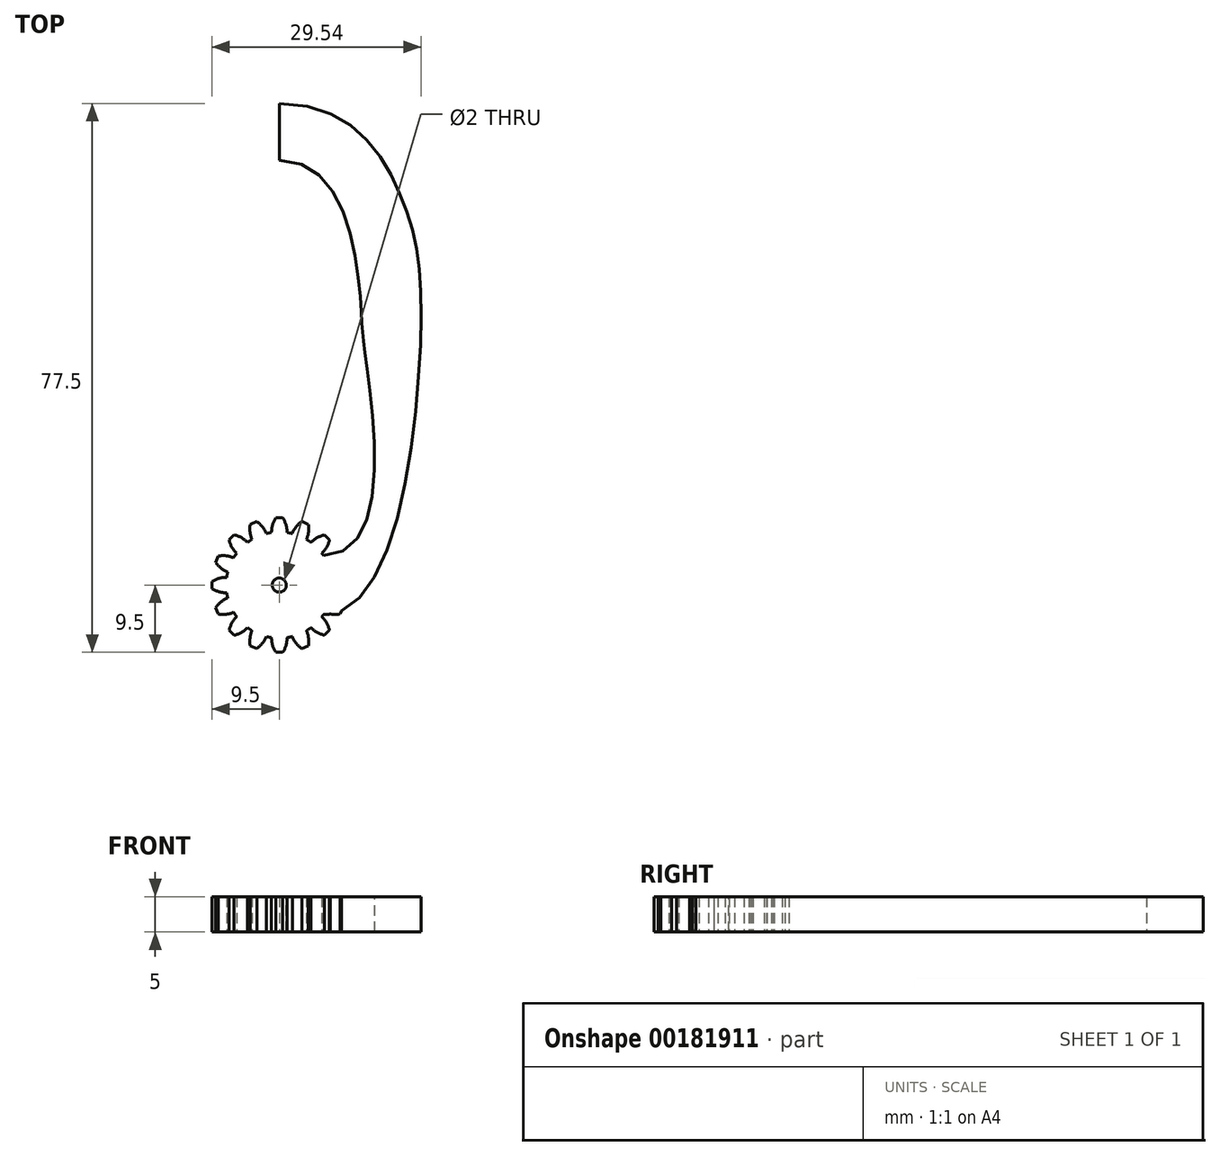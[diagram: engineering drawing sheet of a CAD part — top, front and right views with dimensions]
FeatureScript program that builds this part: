
annotation { "Feature Type Name" : "Feature", "Feature Type Description" : "" }
export const myFeature = defineFeature(function(context is Context, id is Id, definition is map)
    precondition{}
    {
        {
            var Q0;
            Q0=qCreatedBy(makeId("Top.planeOp"),FACE);
            var sketch = newSketch(context, id + "F0", { "sketchPlane" : qUnion([Q0])});
            skCircle(sketch, "E0", {"center": v(0, 0) * mm, "radius": 7.5 * mm});
            skLineSegment(sketch, "E1", {"start": v(0, 0) * mm, "end": v(0, 7.5) * mm, "construction": true});
            skLineSegment(sketch, "E2", {"start": v(0, 9.5) * mm, "end": v(-0.5, 9.5) * mm});
            skArc(sketch, "E3", {"start": v(-0.5, 9.5) * mm, "mid": v(-0.95, 8.5) * mm, "end": v(-1.09, 7.42) * mm});
            skLineSegment(sketch, "E4.MirrorCS", {"start": v(0, 9.5) * mm, "end": v(0.5, 9.5) * mm});
            skArc(sketch, "E5.MirrorCS", {"start": v(0.5, 9.5) * mm, "mid": v(0.95, 8.5) * mm, "end": v(1.09, 7.42) * mm});
            skArc(sketch, "E6.1.0", {"start": v(-4.1, 8.59) * mm, "mid": v(-4.13, 7.5) * mm, "end": v(-3.85, 6.44) * mm});
            skLineSegment(sketch, "E6.1.1", {"start": v(-3.64, 8.78) * mm, "end": v(-4.1, 8.59) * mm});
            skLineSegment(sketch, "E6.1.2", {"start": v(-3.64, 8.78) * mm, "end": v(-3.17, 8.97) * mm});
            skArc(sketch, "E6.1.3", {"start": v(-3.17, 8.97) * mm, "mid": v(-2.38, 8.22) * mm, "end": v(-1.83, 7.27) * mm});
            skArc(sketch, "E6.2.0", {"start": v(-7.07, 6.36) * mm, "mid": v(-6.69, 5.34) * mm, "end": v(-6.02, 4.48) * mm});
            skLineSegment(sketch, "E6.2.1", {"start": v(-6.72, 6.72) * mm, "end": v(-7.07, 6.36) * mm});
            skLineSegment(sketch, "E6.2.2", {"start": v(-6.72, 6.72) * mm, "end": v(-6.36, 7.07) * mm});
            skArc(sketch, "E6.2.3", {"start": v(-6.36, 7.07) * mm, "mid": v(-5.34, 6.69) * mm, "end": v(-4.48, 6.02) * mm});
            skArc(sketch, "E6.3.0", {"start": v(-8.97, 3.17) * mm, "mid": v(-8.22, 2.38) * mm, "end": v(-7.27, 1.83) * mm});
            skLineSegment(sketch, "E6.3.1", {"start": v(-8.78, 3.64) * mm, "end": v(-8.97, 3.17) * mm});
            skLineSegment(sketch, "E6.3.2", {"start": v(-8.78, 3.64) * mm, "end": v(-8.59, 4.1) * mm});
            skArc(sketch, "E6.3.3", {"start": v(-8.59, 4.1) * mm, "mid": v(-7.5, 4.13) * mm, "end": v(-6.44, 3.85) * mm});
            skArc(sketch, "E6.4.0", {"start": v(-9.5, -0.5) * mm, "mid": v(-8.5, -0.95) * mm, "end": v(-7.42, -1.09) * mm});
            skLineSegment(sketch, "E6.4.1", {"start": v(-9.5, 0) * mm, "end": v(-9.5, -0.5) * mm});
            skLineSegment(sketch, "E6.4.2", {"start": v(-9.5, 0) * mm, "end": v(-9.5, 0.5) * mm});
            skArc(sketch, "E6.4.3", {"start": v(-9.5, 0.5) * mm, "mid": v(-8.5, 0.95) * mm, "end": v(-7.42, 1.09) * mm});
            skArc(sketch, "E6.5.0", {"start": v(-8.59, -4.1) * mm, "mid": v(-7.5, -4.13) * mm, "end": v(-6.44, -3.85) * mm});
            skLineSegment(sketch, "E6.5.1", {"start": v(-8.78, -3.64) * mm, "end": v(-8.59, -4.1) * mm});
            skLineSegment(sketch, "E6.5.2", {"start": v(-8.78, -3.64) * mm, "end": v(-8.97, -3.17) * mm});
            skArc(sketch, "E6.5.3", {"start": v(-8.97, -3.17) * mm, "mid": v(-8.22, -2.38) * mm, "end": v(-7.27, -1.83) * mm});
            skArc(sketch, "E6.6.0", {"start": v(-6.36, -7.07) * mm, "mid": v(-5.34, -6.69) * mm, "end": v(-4.48, -6.02) * mm});
            skLineSegment(sketch, "E6.6.1", {"start": v(-6.72, -6.72) * mm, "end": v(-6.36, -7.07) * mm});
            skLineSegment(sketch, "E6.6.2", {"start": v(-6.72, -6.72) * mm, "end": v(-7.07, -6.36) * mm});
            skArc(sketch, "E6.6.3", {"start": v(-7.07, -6.36) * mm, "mid": v(-6.69, -5.34) * mm, "end": v(-6.02, -4.48) * mm});
            skArc(sketch, "E6.7.0", {"start": v(-3.17, -8.97) * mm, "mid": v(-2.38, -8.22) * mm, "end": v(-1.83, -7.27) * mm});
            skLineSegment(sketch, "E6.7.1", {"start": v(-3.64, -8.78) * mm, "end": v(-3.17, -8.97) * mm});
            skLineSegment(sketch, "E6.7.2", {"start": v(-3.64, -8.78) * mm, "end": v(-4.1, -8.59) * mm});
            skArc(sketch, "E6.7.3", {"start": v(-4.1, -8.59) * mm, "mid": v(-4.13, -7.5) * mm, "end": v(-3.85, -6.44) * mm});
            skArc(sketch, "E6.8.0", {"start": v(0.5, -9.5) * mm, "mid": v(0.95, -8.5) * mm, "end": v(1.09, -7.42) * mm});
            skLineSegment(sketch, "E6.8.1", {"start": v(0, -9.5) * mm, "end": v(0.5, -9.5) * mm});
            skLineSegment(sketch, "E6.8.2", {"start": v(0, -9.5) * mm, "end": v(-0.5, -9.5) * mm});
            skArc(sketch, "E6.8.3", {"start": v(-0.5, -9.5) * mm, "mid": v(-0.95, -8.5) * mm, "end": v(-1.09, -7.42) * mm});
            skArc(sketch, "E6.9.0", {"start": v(4.1, -8.59) * mm, "mid": v(4.13, -7.5) * mm, "end": v(3.85, -6.44) * mm});
            skLineSegment(sketch, "E6.9.1", {"start": v(3.64, -8.78) * mm, "end": v(4.1, -8.59) * mm});
            skLineSegment(sketch, "E6.9.2", {"start": v(3.64, -8.78) * mm, "end": v(3.17, -8.97) * mm});
            skArc(sketch, "E6.9.3", {"start": v(3.17, -8.97) * mm, "mid": v(2.38, -8.22) * mm, "end": v(1.83, -7.27) * mm});
            skArc(sketch, "E6.10.0", {"start": v(7.07, -6.36) * mm, "mid": v(6.69, -5.34) * mm, "end": v(6.02, -4.48) * mm});
            skLineSegment(sketch, "E6.10.1", {"start": v(6.72, -6.72) * mm, "end": v(7.07, -6.36) * mm});
            skLineSegment(sketch, "E6.10.2", {"start": v(6.72, -6.72) * mm, "end": v(6.36, -7.07) * mm});
            skArc(sketch, "E6.10.3", {"start": v(6.36, -7.07) * mm, "mid": v(5.34, -6.69) * mm, "end": v(4.48, -6.02) * mm});
            skArc(sketch, "E6.11.0", {"start": v(8.97, -3.17) * mm, "mid": v(8.22, -2.38) * mm, "end": v(7.27, -1.83) * mm});
            skLineSegment(sketch, "E6.11.1", {"start": v(8.78, -3.64) * mm, "end": v(8.97, -3.17) * mm});
            skLineSegment(sketch, "E6.11.2", {"start": v(8.78, -3.64) * mm, "end": v(8.59, -4.1) * mm});
            skArc(sketch, "E6.11.3", {"start": v(8.59, -4.1) * mm, "mid": v(7.5, -4.13) * mm, "end": v(6.44, -3.85) * mm});
            skArc(sketch, "E6.12.0", {"start": v(9.5, 0.5) * mm, "mid": v(8.5, 0.95) * mm, "end": v(7.42, 1.09) * mm});
            skLineSegment(sketch, "E6.12.1", {"start": v(9.5, 0) * mm, "end": v(9.5, 0.5) * mm});
            skLineSegment(sketch, "E6.12.2", {"start": v(9.5, 0) * mm, "end": v(9.5, -0.5) * mm});
            skArc(sketch, "E6.12.3", {"start": v(9.5, -0.5) * mm, "mid": v(8.5, -0.95) * mm, "end": v(7.42, -1.09) * mm});
            skArc(sketch, "E6.13.0", {"start": v(8.59, 4.1) * mm, "mid": v(7.5, 4.13) * mm, "end": v(6.44, 3.85) * mm});
            skLineSegment(sketch, "E6.13.1", {"start": v(8.78, 3.64) * mm, "end": v(8.59, 4.1) * mm});
            skLineSegment(sketch, "E6.13.2", {"start": v(8.78, 3.64) * mm, "end": v(8.97, 3.17) * mm});
            skArc(sketch, "E6.13.3", {"start": v(8.97, 3.17) * mm, "mid": v(8.22, 2.38) * mm, "end": v(7.27, 1.83) * mm});
            skArc(sketch, "E6.14.0", {"start": v(6.36, 7.07) * mm, "mid": v(5.34, 6.69) * mm, "end": v(4.48, 6.02) * mm});
            skLineSegment(sketch, "E6.14.1", {"start": v(6.72, 6.72) * mm, "end": v(6.36, 7.07) * mm});
            skLineSegment(sketch, "E6.14.2", {"start": v(6.72, 6.72) * mm, "end": v(7.07, 6.36) * mm});
            skArc(sketch, "E6.14.3", {"start": v(7.07, 6.36) * mm, "mid": v(6.69, 5.34) * mm, "end": v(6.02, 4.48) * mm});
            skArc(sketch, "E6.15.0", {"start": v(3.17, 8.97) * mm, "mid": v(2.38, 8.22) * mm, "end": v(1.83, 7.27) * mm});
            skLineSegment(sketch, "E6.15.1", {"start": v(3.64, 8.78) * mm, "end": v(3.17, 8.97) * mm});
            skLineSegment(sketch, "E6.15.2", {"start": v(3.64, 8.78) * mm, "end": v(4.1, 8.59) * mm});
            skArc(sketch, "E6.15.3", {"start": v(4.1, 8.59) * mm, "mid": v(4.13, 7.5) * mm, "end": v(3.85, 6.44) * mm});
            skSolve(sketch);
        }
        {
            var Q0;
            Q0=qSketchRegion(id+"F0",true);
            extrude(context, id + "F1", {"entities" : qUnion([Q0]), "depth" : 5 * mm});
        }
        {
            var Q0;
            Q0=makeQuery(id+"F1.opExtrude","CAP_FACE",FACE,{"disambiguationData":[OSD([sQuery(id+"F0.wireOp",EDGE,"E0"),sQuery(id+"F0.wireOp",EDGE,"E2"),sQuery(id+"F0.wireOp",EDGE,"E3"),sQuery(id+"F0.wireOp",EDGE,"E4.MirrorCS"),sQuery(id+"F0.wireOp",EDGE,"E5.MirrorCS"),sQuery(id+"F0.wireOp",EDGE,"E6.1.0"),sQuery(id+"F0.wireOp",EDGE,"E6.1.1"),sQuery(id+"F0.wireOp",EDGE,"E6.1.2"),sQuery(id+"F0.wireOp",EDGE,"E6.1.3"),sQuery(id+"F0.wireOp",EDGE,"E6.2.0"),sQuery(id+"F0.wireOp",EDGE,"E6.2.1"),sQuery(id+"F0.wireOp",EDGE,"E6.2.2"),sQuery(id+"F0.wireOp",EDGE,"E6.2.3"),sQuery(id+"F0.wireOp",EDGE,"E6.3.0"),sQuery(id+"F0.wireOp",EDGE,"E6.3.1"),sQuery(id+"F0.wireOp",EDGE,"E6.3.2"),sQuery(id+"F0.wireOp",EDGE,"E6.3.3"),sQuery(id+"F0.wireOp",EDGE,"E6.4.0"),sQuery(id+"F0.wireOp",EDGE,"E6.4.1"),sQuery(id+"F0.wireOp",EDGE,"E6.4.2"),sQuery(id+"F0.wireOp",EDGE,"E6.4.3"),sQuery(id+"F0.wireOp",EDGE,"E6.5.0"),sQuery(id+"F0.wireOp",EDGE,"E6.5.1"),sQuery(id+"F0.wireOp",EDGE,"E6.5.2"),sQuery(id+"F0.wireOp",EDGE,"E6.5.3"),sQuery(id+"F0.wireOp",EDGE,"E6.6.0"),sQuery(id+"F0.wireOp",EDGE,"E6.6.1"),sQuery(id+"F0.wireOp",EDGE,"E6.6.2"),sQuery(id+"F0.wireOp",EDGE,"E6.6.3"),sQuery(id+"F0.wireOp",EDGE,"E6.7.0"),sQuery(id+"F0.wireOp",EDGE,"E6.7.1"),sQuery(id+"F0.wireOp",EDGE,"E6.7.2"),sQuery(id+"F0.wireOp",EDGE,"E6.7.3"),sQuery(id+"F0.wireOp",EDGE,"E6.8.0"),sQuery(id+"F0.wireOp",EDGE,"E6.8.1"),sQuery(id+"F0.wireOp",EDGE,"E6.8.2"),sQuery(id+"F0.wireOp",EDGE,"E6.8.3"),sQuery(id+"F0.wireOp",EDGE,"E6.9.0"),sQuery(id+"F0.wireOp",EDGE,"E6.9.1"),sQuery(id+"F0.wireOp",EDGE,"E6.9.2"),sQuery(id+"F0.wireOp",EDGE,"E6.9.3"),sQuery(id+"F0.wireOp",EDGE,"E6.10.0"),sQuery(id+"F0.wireOp",EDGE,"E6.10.1"),sQuery(id+"F0.wireOp",EDGE,"E6.10.2"),sQuery(id+"F0.wireOp",EDGE,"E6.10.3"),sQuery(id+"F0.wireOp",EDGE,"E6.11.0"),sQuery(id+"F0.wireOp",EDGE,"E6.11.1"),sQuery(id+"F0.wireOp",EDGE,"E6.11.2"),sQuery(id+"F0.wireOp",EDGE,"E6.11.3"),sQuery(id+"F0.wireOp",EDGE,"E6.12.0"),sQuery(id+"F0.wireOp",EDGE,"E6.12.1"),sQuery(id+"F0.wireOp",EDGE,"E6.12.2"),sQuery(id+"F0.wireOp",EDGE,"E6.12.3"),sQuery(id+"F0.wireOp",EDGE,"E6.13.0"),sQuery(id+"F0.wireOp",EDGE,"E6.13.1"),sQuery(id+"F0.wireOp",EDGE,"E6.13.2"),sQuery(id+"F0.wireOp",EDGE,"E6.13.3"),sQuery(id+"F0.wireOp",EDGE,"E6.14.0"),sQuery(id+"F0.wireOp",EDGE,"E6.14.1"),sQuery(id+"F0.wireOp",EDGE,"E6.14.2"),sQuery(id+"F0.wireOp",EDGE,"E6.14.3"),sQuery(id+"F0.wireOp",EDGE,"E6.15.0"),sQuery(id+"F0.wireOp",EDGE,"E6.15.1"),sQuery(id+"F0.wireOp",EDGE,"E6.15.2"),sQuery(id+"F0.wireOp",EDGE,"E6.15.3")])],"isStart":false});
            var sketch = newSketch(context, id + "F2", { "sketchPlane" : qUnion([Q0])});
            skCircle(sketch, "E7", {"center": v(0, 0) * mm, "radius": 1 * mm});
            skSolve(sketch);
        }
        {
            var Q0;
            Q0=qSketchRegion(id+"F2",true);
            extrude(context, id + "F3", {"entities" : qUnion([Q0]), "operationType" : NewBodyOperationType.REMOVE, "endBound" : BoundingType.THROUGH_ALL, "oppositeDirection" : true, "depth" : 25 * mm});
        }
        {
            var Q0;
            Q0=qCreatedBy(makeId("Top.planeOp"),FACE);
            var sketch = newSketch(context, id + "F4", { "sketchPlane" : qUnion([Q0])});
            skLineSegment(sketch, "E8", {"start": v(0, 60) * mm, "end": v(0, 68) * mm});
            skFitSpline(sketch, "E9", {"points": [v(0, 60) * mm, v(11.53, 39.23) * mm, v(12.27, 31.6) * mm, v(6.24, 4.17) * mm], "startDerivative": vector(79.67, 0) * mm, "endDerivative": vector(-73.28, 0) * mm});
            skFitSpline(sketch, "E10", {"points": [v(0, 68) * mm, v(17.03, 55.23) * mm, v(19.87, 32.6) * mm, v(6.24, -4.17) * mm], "startDerivative": vector(101.77, 0) * mm, "endDerivative": vector(-74.98, 0) * mm});
            skLineSegment(sketch, "E11", {"start": v(6.24, 4.17) * mm, "end": v(6.24, -4.17) * mm});
            skSolve(sketch);
        }
        {
            var Q0;
            Q0 = qSketchRegion(id + "F4", true);
            var Q1;
            Q1=makeQuery(id+"F1.opExtrude","CAP_FACE",FACE,{"disambiguationData":[OSD([sQuery(id+"F0.wireOp",EDGE,"E0"),sQuery(id+"F0.wireOp",EDGE,"E2"),sQuery(id+"F0.wireOp",EDGE,"E3"),sQuery(id+"F0.wireOp",EDGE,"E4.MirrorCS"),sQuery(id+"F0.wireOp",EDGE,"E5.MirrorCS"),sQuery(id+"F0.wireOp",EDGE,"E6.1.0"),sQuery(id+"F0.wireOp",EDGE,"E6.1.1"),sQuery(id+"F0.wireOp",EDGE,"E6.1.2"),sQuery(id+"F0.wireOp",EDGE,"E6.1.3"),sQuery(id+"F0.wireOp",EDGE,"E6.2.0"),sQuery(id+"F0.wireOp",EDGE,"E6.2.1"),sQuery(id+"F0.wireOp",EDGE,"E6.2.2"),sQuery(id+"F0.wireOp",EDGE,"E6.2.3"),sQuery(id+"F0.wireOp",EDGE,"E6.3.0"),sQuery(id+"F0.wireOp",EDGE,"E6.3.1"),sQuery(id+"F0.wireOp",EDGE,"E6.3.2"),sQuery(id+"F0.wireOp",EDGE,"E6.3.3"),sQuery(id+"F0.wireOp",EDGE,"E6.4.0"),sQuery(id+"F0.wireOp",EDGE,"E6.4.1"),sQuery(id+"F0.wireOp",EDGE,"E6.4.2"),sQuery(id+"F0.wireOp",EDGE,"E6.4.3"),sQuery(id+"F0.wireOp",EDGE,"E6.5.0"),sQuery(id+"F0.wireOp",EDGE,"E6.5.1"),sQuery(id+"F0.wireOp",EDGE,"E6.5.2"),sQuery(id+"F0.wireOp",EDGE,"E6.5.3"),sQuery(id+"F0.wireOp",EDGE,"E6.6.0"),sQuery(id+"F0.wireOp",EDGE,"E6.6.1"),sQuery(id+"F0.wireOp",EDGE,"E6.6.2"),sQuery(id+"F0.wireOp",EDGE,"E6.6.3"),sQuery(id+"F0.wireOp",EDGE,"E6.7.0"),sQuery(id+"F0.wireOp",EDGE,"E6.7.1"),sQuery(id+"F0.wireOp",EDGE,"E6.7.2"),sQuery(id+"F0.wireOp",EDGE,"E6.7.3"),sQuery(id+"F0.wireOp",EDGE,"E6.8.0"),sQuery(id+"F0.wireOp",EDGE,"E6.8.1"),sQuery(id+"F0.wireOp",EDGE,"E6.8.2"),sQuery(id+"F0.wireOp",EDGE,"E6.8.3"),sQuery(id+"F0.wireOp",EDGE,"E6.9.0"),sQuery(id+"F0.wireOp",EDGE,"E6.9.1"),sQuery(id+"F0.wireOp",EDGE,"E6.9.2"),sQuery(id+"F0.wireOp",EDGE,"E6.9.3"),sQuery(id+"F0.wireOp",EDGE,"E6.10.0"),sQuery(id+"F0.wireOp",EDGE,"E6.10.1"),sQuery(id+"F0.wireOp",EDGE,"E6.10.2"),sQuery(id+"F0.wireOp",EDGE,"E6.10.3"),sQuery(id+"F0.wireOp",EDGE,"E6.11.0"),sQuery(id+"F0.wireOp",EDGE,"E6.11.1"),sQuery(id+"F0.wireOp",EDGE,"E6.11.2"),sQuery(id+"F0.wireOp",EDGE,"E6.11.3"),sQuery(id+"F0.wireOp",EDGE,"E6.12.0"),sQuery(id+"F0.wireOp",EDGE,"E6.12.1"),sQuery(id+"F0.wireOp",EDGE,"E6.12.2"),sQuery(id+"F0.wireOp",EDGE,"E6.12.3"),sQuery(id+"F0.wireOp",EDGE,"E6.13.0"),sQuery(id+"F0.wireOp",EDGE,"E6.13.1"),sQuery(id+"F0.wireOp",EDGE,"E6.13.2"),sQuery(id+"F0.wireOp",EDGE,"E6.13.3"),sQuery(id+"F0.wireOp",EDGE,"E6.14.0"),sQuery(id+"F0.wireOp",EDGE,"E6.14.1"),sQuery(id+"F0.wireOp",EDGE,"E6.14.2"),sQuery(id+"F0.wireOp",EDGE,"E6.14.3"),sQuery(id+"F0.wireOp",EDGE,"E6.15.0"),sQuery(id+"F0.wireOp",EDGE,"E6.15.1"),sQuery(id+"F0.wireOp",EDGE,"E6.15.2"),sQuery(id+"F0.wireOp",EDGE,"E6.15.3")])],"isStart":false});
            extrude(context, id + "F5", {"entities" : qUnion([Q0]), "operationType" : NewBodyOperationType.ADD, "endBound" : BoundingType.UP_TO_SURFACE, "endBoundEntityFace" : qUnion([Q1]), "depth" : 25 * mm});
        }
    });
